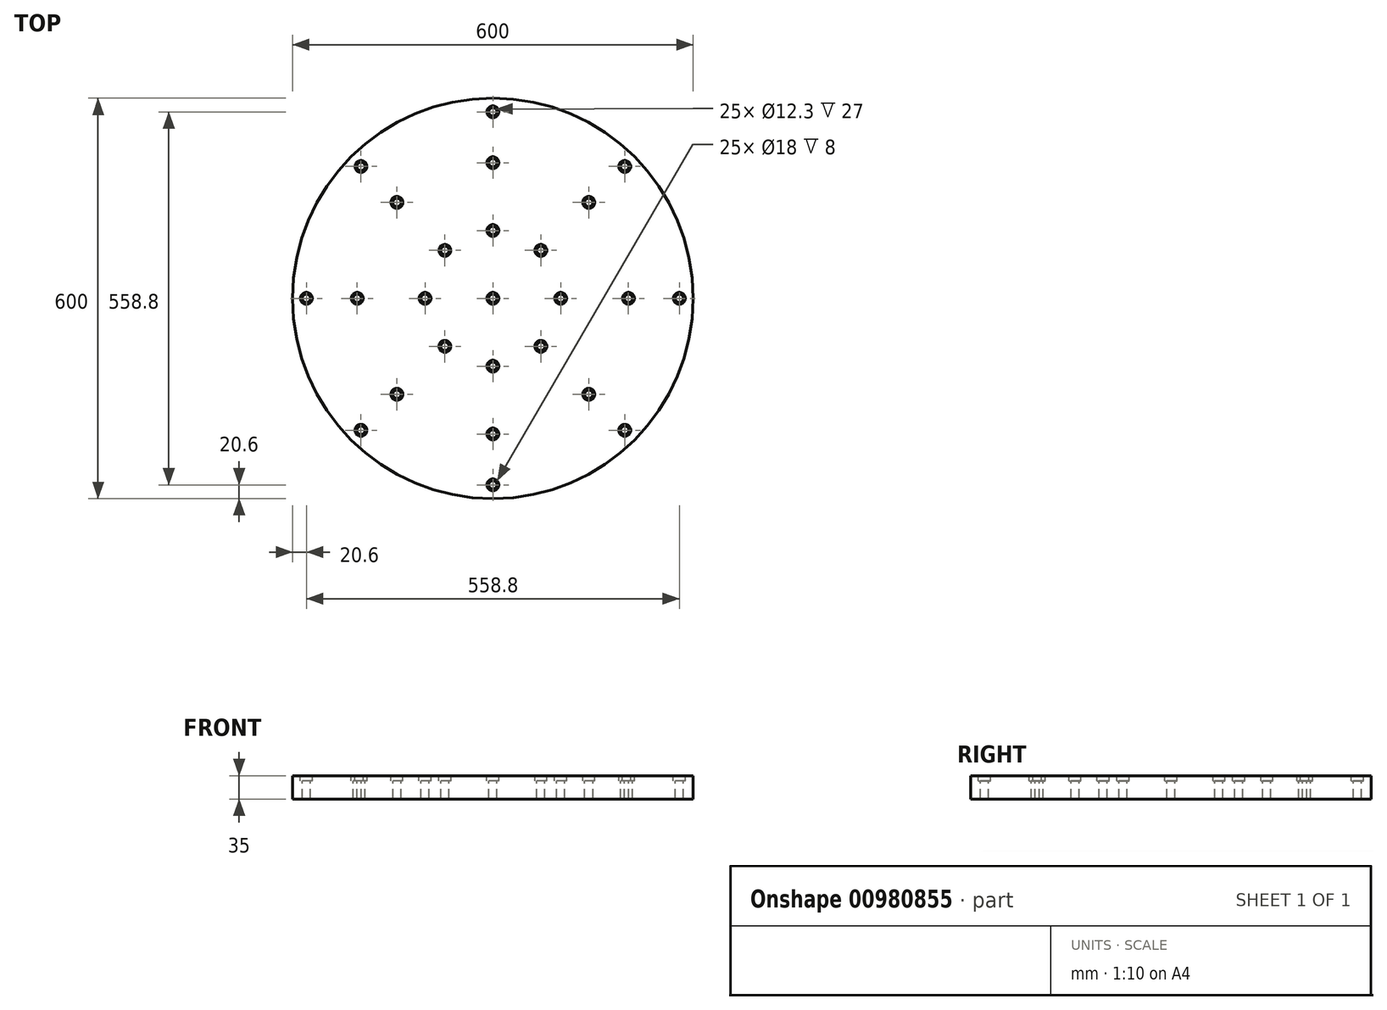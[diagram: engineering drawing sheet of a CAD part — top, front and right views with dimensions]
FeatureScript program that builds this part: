
annotation { "Feature Type Name" : "Feature", "Feature Type Description" : "" }
export const myFeature = defineFeature(function(context is Context, id is Id, definition is map)
    precondition{}
    {
        {
            var Q0;
            Q0=qCreatedBy(makeId("Front.planeOp"),FACE);
            var sketch = newSketch(context, id + "F0", { "sketchPlane" : qUnion([Q0])});
            skLineSegment(sketch, "E0.bottom", {"start": v(300, 17.5) * mm, "end": v(-300, 17.5) * mm});
            skLineSegment(sketch, "E0.top", {"start": v(300, -17.5) * mm, "end": v(-300, -17.5) * mm});
            skLineSegment(sketch, "E0.left", {"start": v(300, 17.5) * mm, "end": v(300, -17.5) * mm});
            skLineSegment(sketch, "E0.right", {"start": v(-300, 17.5) * mm, "end": v(-300, -17.5) * mm});
            skPoint(sketch, "E0.middle", {"position": v(0, 0) * mm});
            skLineSegment(sketch, "E1", {"start": v(0, -17.5) * mm, "end": v(0, 17.5) * mm});
            skSolve(sketch);
        }
        {
            var Q0;
            {var subQ0=sQuery(id+"F0.wireOp",EDGE,"E0.left");Q0=makeQuery(id+"F0.imprint","IMPRINT",FACE,{"disambiguationData":[TD([[makeQuery(id+"F0.imprint","IMPRINT",EDGE,{"derivedFrom":subQ0}),-1.0]])]});}
            var Q1;
            Q1=sQuery(id+"F0.wireOp",EDGE,"E1");
            revolve(context, id + "F1", {"surfaceOperationType" : NewSurfaceOperationType.NEW, "entities" : qUnion([Q0]), "axis" : qUnion([Q1]), "revolveType" : RevolveType.FULL});
        }
        {
            var Q0;
            Q0=makeQuery(id+"F1.opRevolve","SWEPT_FACE",FACE,{"disambiguationData":[OSD([sQuery(id+"F0.wireOp",EDGE,"E0.bottom")])]});
            var sketch = newSketch(context, id + "F2", { "sketchPlane" : qUnion([Q0])});
            skCircle(sketch, "E2", {"center": v(0, 0) * mm, "radius": 101.6 * mm});
            skCircle(sketch, "E3", {"center": v(0, 0) * mm, "radius": 203.2 * mm});
            skCircle(sketch, "E4", {"center": v(0, 0) * mm, "radius": 279.4 * mm});
            skLineSegment(sketch, "E5", {"start": v(0, 0) * mm, "end": v(300, 0) * mm});
            skLineSegment(sketch, "E6", {"start": v(0, 0) * mm, "end": v(212.13, 212.13) * mm});
            skPoint(sketch, "E7", {"position": v(101.6, 0) * mm});
            skPoint(sketch, "E8", {"position": v(203.2, 0) * mm});
            skPoint(sketch, "E9", {"position": v(279.4, 0) * mm});
            skPoint(sketch, "E10", {"position": v(71.84, 71.84) * mm});
            skPoint(sketch, "E11", {"position": v(143.68, 143.68) * mm});
            skPoint(sketch, "E12", {"position": v(197.57, 197.57) * mm});
            skLineSegment(sketch, "E13", {"start": v(0, 0) * mm, "end": v(0, 300) * mm});
            skLineSegment(sketch, "E14", {"start": v(0, 300) * mm, "end": v(0, 279.4) * mm});
            skLineSegment(sketch, "E15", {"start": v(0, 279.4) * mm, "end": v(0, 203.2) * mm});
            skLineSegment(sketch, "E16", {"start": v(0, 203.2) * mm, "end": v(0, 101.6) * mm});
            skLineSegment(sketch, "E17", {"start": v(0, 0) * mm, "end": v(-300, 0) * mm});
            skLineSegment(sketch, "E18", {"start": v(-300, 0) * mm, "end": v(-279.4, 0) * mm});
            skLineSegment(sketch, "E19", {"start": v(-279.4, 0) * mm, "end": v(-203.2, 0) * mm});
            skLineSegment(sketch, "E20", {"start": v(-203.2, 0) * mm, "end": v(-101.6, 0) * mm});
            skLineSegment(sketch, "E21", {"start": v(-101.6, 0) * mm, "end": v(0, 0) * mm});
            skLineSegment(sketch, "E22", {"start": v(0, -300) * mm, "end": v(0, -279.4) * mm});
            skLineSegment(sketch, "E23", {"start": v(0, -279.4) * mm, "end": v(0, -203.2) * mm});
            skLineSegment(sketch, "E24", {"start": v(0, -203.2) * mm, "end": v(0, -101.6) * mm});
            skLineSegment(sketch, "E25", {"start": v(0, -101.6) * mm, "end": v(0, 0) * mm});
            skLineSegment(sketch, "E26", {"start": v(0, 0) * mm, "end": v(212.13, -212.13) * mm});
            skPoint(sketch, "E27", {"position": v(71.84, -71.84) * mm});
            skPoint(sketch, "E28", {"position": v(143.68, -143.68) * mm});
            skPoint(sketch, "E29", {"position": v(197.57, -197.57) * mm});
            skPoint(sketch, "E30", {"position": v(0, -279.4) * mm});
            skPoint(sketch, "E31", {"position": v(0, -203.2) * mm});
            skPoint(sketch, "E32", {"position": v(0, -101.6) * mm});
            skPoint(sketch, "E33", {"position": v(-101.6, 0) * mm});
            skPoint(sketch, "E34", {"position": v(-203.2, 0) * mm});
            skPoint(sketch, "E35", {"position": v(-279.4, 0) * mm});
            skPoint(sketch, "E36", {"position": v(0, 101.6) * mm});
            skPoint(sketch, "E37", {"position": v(0, 203.2) * mm});
            skPoint(sketch, "E38", {"position": v(0, 279.4) * mm});
            skLineSegment(sketch, "E39.MirrorCS", {"start": v(0, 0) * mm, "end": v(-212.13, 212.13) * mm});
            skLineSegment(sketch, "E40.MirrorCS", {"start": v(0, 0) * mm, "end": v(-212.13, -212.13) * mm});
            skPoint(sketch, "E41", {"position": v(-143.68, 143.68) * mm});
            skPoint(sketch, "E42", {"position": v(-197.57, 197.57) * mm});
            skPoint(sketch, "E43", {"position": v(-71.84, 71.84) * mm});
            skPoint(sketch, "E44", {"position": v(-71.84, -71.84) * mm});
            skPoint(sketch, "E45", {"position": v(-143.68, -143.68) * mm});
            skPoint(sketch, "E46", {"position": v(-197.57, -197.57) * mm});
            skSolve(sketch);
        }
        {
            var Q0;
            Q0=sQuery(id+"F2.wireOp",VERTEX,"E42");
            var Q1;
            Q1=sQuery(id+"F2.wireOp",VERTEX,"E38");
            var Q2;
            Q2=sQuery(id+"F2.wireOp",VERTEX,"E12");
            var Q3;
            Q3=sQuery(id+"F2.wireOp",VERTEX,"E9");
            var Q4;
            Q4=sQuery(id+"F2.wireOp",VERTEX,"E29");
            var Q5;
            Q5=sQuery(id+"F2.wireOp",VERTEX,"E30");
            var Q6;
            Q6=sQuery(id+"F2.wireOp",VERTEX,"E46");
            var Q7;
            Q7=sQuery(id+"F2.wireOp",VERTEX,"E35");
            var Q8;
            Q8=sQuery(id+"F2.wireOp",VERTEX,"E34");
            var Q9;
            Q9=sQuery(id+"F2.wireOp",VERTEX,"E45");
            var Q10;
            Q10=sQuery(id+"F2.wireOp",VERTEX,"E31");
            var Q11;
            Q11=sQuery(id+"F2.wireOp",VERTEX,"E28");
            var Q12;
            Q12=sQuery(id+"F2.wireOp",VERTEX,"E8");
            var Q13;
            Q13=sQuery(id+"F2.wireOp",VERTEX,"E11");
            var Q14;
            Q14=sQuery(id+"F2.wireOp",VERTEX,"E37");
            var Q15;
            Q15=sQuery(id+"F2.wireOp",VERTEX,"E41");
            var Q16;
            Q16=sQuery(id+"F2.wireOp",VERTEX,"E43");
            var Q17;
            Q17=sQuery(id+"F2.wireOp",VERTEX,"E36");
            var Q18;
            Q18=sQuery(id+"F2.wireOp",VERTEX,"E10");
            var Q19;
            Q19=sQuery(id+"F2.wireOp",VERTEX,"E7");
            var Q20;
            Q20=sQuery(id+"F2.wireOp",VERTEX,"E27");
            var Q21;
            Q21=sQuery(id+"F2.wireOp",VERTEX,"E32");
            var Q22;
            Q22=sQuery(id+"F2.wireOp",VERTEX,"E44");
            var Q23;
            Q23=sQuery(id+"F2.wireOp",VERTEX,"E33");
            var Q24;
            Q24=sQuery(id+"F2.wireOp",VERTEX,"E5.start");
            var Q25;
            Q25=makeQuery(id+"F1.opRevolve","SWEPT_BODY",BODY,{"disambiguationData":[OSD([sQuery(id+"F0.wireOp",EDGE,"E0.bottom"),sQuery(id+"F0.wireOp",EDGE,"E0.top"),sQuery(id+"F0.wireOp",EDGE,"E0.left"),sQuery(id+"F0.wireOp",EDGE,"E1")])]});
            hole(context, id + "F3", {"style" : HoleStyle.C_BORE, "endStyle" : HoleEndStyle.BLIND, "holeDiameter" : 12.3 * mm, "cBoreDiameter" : 18 * mm, "cBoreDepth" : 8 * mm, "majorDiameter" : 6.35 * mm, "holeDepth" : 35 * mm, "isTappedThrough" : true, "tappedDepth" : 12.7 * mm, "tapClearance" : 3, "locations" : qUnion([Q0, Q1, Q2, Q3, Q4, Q5, Q6, Q7, Q8, Q9, Q10, Q11, Q12, Q13, Q14, Q15, Q16, Q17, Q18, Q19, Q20, Q21, Q22, Q23, Q24]), "scope" : qUnion([Q25])});
        }
    });
